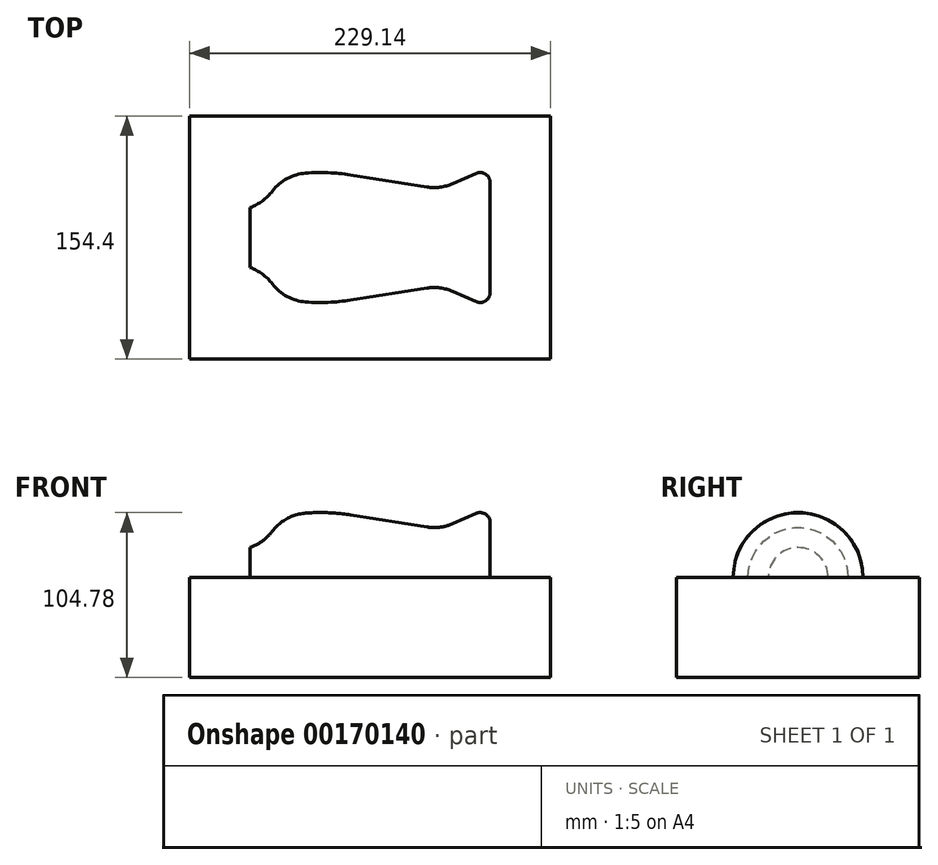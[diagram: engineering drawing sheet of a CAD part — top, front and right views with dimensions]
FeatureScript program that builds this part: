
annotation { "Feature Type Name" : "Feature", "Feature Type Description" : "" }
export const myFeature = defineFeature(function(context is Context, id is Id, definition is map)
    precondition{}
    {
        {
            var Q0;
            Q0=qCreatedBy(makeId("Top.planeOp"),FACE);
            var sketch = newSketch(context, id + "F0", { "sketchPlane" : qUnion([Q0])});
            skLineSegment(sketch, "E0", {"start": v(-76.2, 0) * mm, "end": v(76.2, 0) * mm});
            skLineSegment(sketch, "E1", {"start": v(-76.2, 0) * mm, "end": v(-76.2, 19.05) * mm, "construction": true});
            skLineSegment(sketch, "E2", {"start": v(-76.2, 19.05) * mm, "end": v(76.2, 19.05) * mm, "construction": true});
            skLineSegment(sketch, "E3", {"start": v(-76.2, 19.05) * mm, "end": v(-76.2, 41.28) * mm, "construction": true});
            skLineSegment(sketch, "E4", {"start": v(-76.2, 41.28) * mm, "end": v(76.2, 41.27) * mm, "construction": true});
            skPoint(sketch, "E5", {"position": v(-31.75, 41.28) * mm});
            skLineSegment(sketch, "E6", {"start": v(76.2, 0) * mm, "end": v(76.2, 19.05) * mm, "construction": true});
            skLineSegment(sketch, "E7", {"start": v(-76.2, 31.75) * mm, "end": v(76.2, 31.75) * mm, "construction": true});
            skLineSegment(sketch, "E8", {"start": v(76.2, 19.05) * mm, "end": v(76.2, 41.28) * mm, "construction": true});
            skPoint(sketch, "E9", {"position": v(40.64, 31.75) * mm});
            skLineSegment(sketch, "E10", {"start": v(76.2, 0) * mm, "end": v(76.2, 34.92) * mm});
            skArc(sketch, "E11", {"start": v(76.2, 34.92) * mm, "mid": v(73.32, 40.24) * mm, "end": v(67.3, 40.74) * mm});
            skLineSegment(sketch, "E12", {"start": v(52.5, 34.24) * mm, "end": v(67.3, 40.74) * mm});
            skArc(sketch, "E13", {"start": v(36.05, 32.1) * mm, "mid": v(44.43, 32) * mm, "end": v(52.5, 34.24) * mm});
            skArc(sketch, "E14", {"start": v(-12.58, 39.77) * mm, "mid": v(-26.72, 41.17) * mm, "end": v(-40.93, 40.93) * mm});
            skLineSegment(sketch, "E15", {"start": v(-76.2, 41.28) * mm, "end": v(-76.2, 0) * mm});
            skArc(sketch, "E16", {"start": v(-76.2, 19.05) * mm, "mid": v(-68.38, 23.3) * mm, "end": v(-62.03, 29.54) * mm});
            skArc(sketch, "E17", {"start": v(-40.93, 40.93) * mm, "mid": v(-52.7, 37.49) * mm, "end": v(-62.03, 29.54) * mm});
            skLineSegment(sketch, "E18", {"start": v(-12.58, 39.77) * mm, "end": v(36.05, 32.1) * mm});
            skSolve(sketch);
        }
        {
            var Q0;
            Q0=makeQuery(id+"F0.imprint","IMPRINT",FACE,{"disambiguationData":[TD([[makeQuery(id+"F0.imprint","IMPRINT",EDGE,{"derivedFrom":sQuery(id+"F0.wireOp",EDGE,"E0")}),1.0]])]});
            var Q1;
            Q1=sQuery(id+"F0.wireOp",EDGE,"E0");
            revolve(context, id + "F1", {"entities" : qUnion([Q0]), "axis" : qUnion([Q1]), "revolveType" : RevolveType.FULL});
        }
        {
            var Q0;
            Q0=qCreatedBy(makeId("Top.planeOp"),FACE);
            var sketch = newSketch(context, id + "F2", { "sketchPlane" : qUnion([Q0])});
            skLineSegment(sketch, "E19.bottom", {"start": v(114.57, 77.2) * mm, "end": v(-114.57, 77.2) * mm});
            skLineSegment(sketch, "E19.top", {"start": v(114.57, -77.2) * mm, "end": v(-114.57, -77.2) * mm});
            skLineSegment(sketch, "E19.left", {"start": v(114.57, 77.2) * mm, "end": v(114.57, -77.2) * mm});
            skLineSegment(sketch, "E19.right", {"start": v(-114.57, 77.2) * mm, "end": v(-114.57, -77.2) * mm});
            skPoint(sketch, "E19.middle", {"position": v(0, 0) * mm});
            skSolve(sketch);
        }
        {
            var Q0;
            Q0=qSketchRegion(id+"F2",true);
            extrude(context, id + "F3", {"entities" : qUnion([Q0]), "operationType" : NewBodyOperationType.ADD, "oppositeDirection" : true, "depth" : 63.5 * mm});
        }
    });
